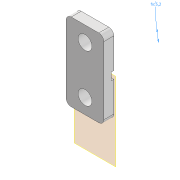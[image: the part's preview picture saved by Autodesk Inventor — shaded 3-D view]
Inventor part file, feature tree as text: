
AUTODESK INVENTOR PART (.ipt)
format: ipt  version: 2020 (Build 240168000, 168)  size: 108,032 bytes
history: native  units: mm
features: other x5, extrude x2, sketch x1, fillet x1
ambient origin geometry x8: Origin, YZ Plane, XZ Plane, XY Plane, X Axis, Y Axis, Z Axis, Center Point
bodies: Body1 (feature_tree)
feature tree (9):
  other  "Sólido1"
  other  "Plano de trabalho1"
  sketch  "Esboço1"  dims[d0=14.0mm d1=14.0mm d2=4.0mm d3=0.0mm d4=1.0mm d5=0.0mm d6=2.0mm d7=5.2mm d8=5.2mm]
  extrude  "Extrusão1"  Depth=14.0mm
  extrude  "Extrusão2"  Depth=4.0mm TaperAngle=0.0deg
  fillet  "Arredondamento1"  Radius=1.0mm
  other  "<userpath>\OneDrive\Área de Trabalho\Calorimetro 2022\Inventor\Montagem_suporte_termopar.iam"
  other  "Montagem_suporte_termopar.iam"
  other  "suporte_termopar_al:1"
